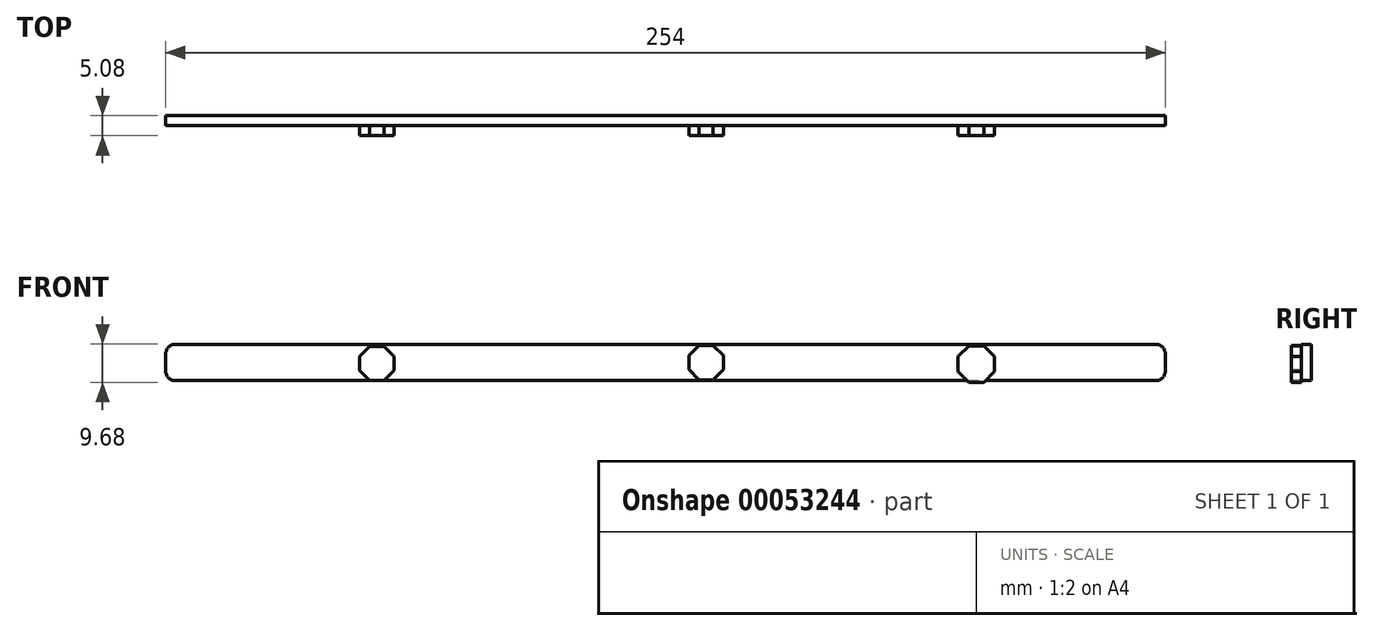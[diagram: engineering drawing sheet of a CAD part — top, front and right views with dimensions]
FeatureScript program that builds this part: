
annotation { "Feature Type Name" : "Feature", "Feature Type Description" : "" }
export const myFeature = defineFeature(function(context is Context, id is Id, definition is map)
    precondition{}
    {
        {
            var Q0;
            Q0=qCreatedBy(makeId("Front.planeOp"),FACE);
            var sketch = newSketch(context, id + "F0", { "sketchPlane" : qUnion([Q0])});
            skLineSegment(sketch, "E0.bottom", {"start": v(-129.82, 37.82) * mm, "end": v(124.18, 37.82) * mm});
            skLineSegment(sketch, "E0.top", {"start": v(-129.82, 28.55) * mm, "end": v(124.18, 28.55) * mm});
            skLineSegment(sketch, "E0.left", {"start": v(-129.82, 37.82) * mm, "end": v(-129.82, 28.55) * mm});
            skLineSegment(sketch, "E0.right", {"start": v(124.18, 37.82) * mm, "end": v(124.18, 28.55) * mm});
            skSolve(sketch);
        }
        {
            var Q0;
            Q0=makeQuery(id+"F0.imprint","IMPRINT",FACE,{"disambiguationData":[TD([[makeQuery(id+"F0.imprint","IMPRINT",EDGE,{"derivedFrom":sQuery(id+"F0.wireOp",EDGE,"E0.bottom")}),-1.0]])]});
            extrude(context, id + "F1", {"entities" : qUnion([Q0]), "depth" : 2.54 * mm});
        }
        {
            var Q0;
            Q0=makeQuery(id+"F1.opExtrude","SWEPT_EDGE",EDGE,{"disambiguationData":[OSD([sQuery(id+"F0.wireOp",EDGE,"E0.bottom"),sQuery(id+"F0.wireOp",EDGE,"E0.right")])]});
            var Q1;
            Q1=makeQuery(id+"F1.opExtrude","SWEPT_EDGE",EDGE,{"disambiguationData":[OSD([sQuery(id+"F0.wireOp",EDGE,"E0.top"),sQuery(id+"F0.wireOp",EDGE,"E0.right")])]});
            var Q2;
            Q2=makeQuery(id+"F1.opExtrude","SWEPT_EDGE",EDGE,{"disambiguationData":[OSD([sQuery(id+"F0.wireOp",EDGE,"E0.bottom"),sQuery(id+"F0.wireOp",EDGE,"E0.left")])]});
            var Q3;
            Q3=makeQuery(id+"F1.opExtrude","SWEPT_EDGE",EDGE,{"disambiguationData":[OSD([sQuery(id+"F0.wireOp",EDGE,"E0.top"),sQuery(id+"F0.wireOp",EDGE,"E0.left")])]});
            fillet(context, id + "F2", {"entities" : qUnion([Q0, Q1, Q2, Q3]), "radius" : 2.54 * mm, "tangentPropagation" : true, "allowEdgeOverflow" : false});
        }
        {
            var Q0;
            Q0=makeQuery(id+"F1.opExtrude","CAP_FACE",FACE,{"disambiguationData":[OSD([sQuery(id+"F0.wireOp",EDGE,"E0.bottom"),sQuery(id+"F0.wireOp",EDGE,"E0.top"),sQuery(id+"F0.wireOp",EDGE,"E0.left"),sQuery(id+"F0.wireOp",EDGE,"E0.right")])],"isStart":false});
            var sketch = newSketch(context, id + "F3", { "sketchPlane" : qUnion([Q0])});
            skCircle(sketch, "E1.cCircle", {"center": v(-76.18, 32.92) * mm, "radius": 4.37 * mm, "construction": true});
            skLineSegment(sketch, "E1.0", {"start": v(-74.37, 28.55) * mm, "end": v(-78, 28.55) * mm});
            skLineSegment(sketch, "E1.1", {"start": v(-78, 28.55) * mm, "end": v(-80.55, 31.1) * mm});
            skLineSegment(sketch, "E1.2", {"start": v(-80.55, 31.1) * mm, "end": v(-80.55, 34.73) * mm});
            skLineSegment(sketch, "E1.3", {"start": v(-80.55, 34.73) * mm, "end": v(-78, 37.3) * mm});
            skLineSegment(sketch, "E1.4", {"start": v(-78, 37.3) * mm, "end": v(-74.37, 37.3) * mm});
            skLineSegment(sketch, "E1.5", {"start": v(-74.37, 37.3) * mm, "end": v(-71.8, 34.73) * mm});
            skLineSegment(sketch, "E1.6", {"start": v(-71.8, 34.73) * mm, "end": v(-71.8, 31.1) * mm});
            skLineSegment(sketch, "E1.7", {"start": v(-71.8, 31.1) * mm, "end": v(-74.37, 28.55) * mm});
            skPoint(sketch, "E1.0.midPoint", {"position": v(-76.18, 28.55) * mm});
            skSolve(sketch);
        }
        {
            var Q0;
            {var subQ7=sQuery(id+"F3.wireOp",EDGE,"E1.1");Q0=makeQuery(id+"F3.imprint","IMPRINT",FACE,{"disambiguationData":[TD([[makeQuery(id+"F3.imprint","IMPRINT",EDGE,{"derivedFrom":subQ7}),1.0]])]});}
            var sketch = newSketch(context, id + "F4", { "sketchPlane" : qUnion([Q0])});
            skCircle(sketch, "E2.cCircle", {"center": v(7.47, 33.16) * mm, "radius": 4.38 * mm, "construction": true});
            skLineSegment(sketch, "E2.0", {"start": v(9.28, 28.78) * mm, "end": v(5.66, 28.78) * mm});
            skLineSegment(sketch, "E2.1", {"start": v(5.66, 28.78) * mm, "end": v(3.1, 31.35) * mm});
            skLineSegment(sketch, "E2.2", {"start": v(3.1, 31.35) * mm, "end": v(3.1, 34.97) * mm});
            skLineSegment(sketch, "E2.3", {"start": v(3.1, 34.97) * mm, "end": v(5.66, 37.54) * mm});
            skLineSegment(sketch, "E2.4", {"start": v(5.66, 37.54) * mm, "end": v(9.28, 37.54) * mm});
            skLineSegment(sketch, "E2.5", {"start": v(9.28, 37.54) * mm, "end": v(11.85, 34.97) * mm});
            skLineSegment(sketch, "E2.6", {"start": v(11.85, 34.97) * mm, "end": v(11.85, 31.35) * mm});
            skLineSegment(sketch, "E2.7", {"start": v(11.85, 31.35) * mm, "end": v(9.28, 28.78) * mm});
            skPoint(sketch, "E2.0.midPoint", {"position": v(7.47, 28.78) * mm});
            skSolve(sketch);
        }
        {
            var Q0;
            Q0=makeQuery(id+"F4.imprint","IMPRINT",FACE,{"disambiguationData":[TD([[makeQuery(id+"F4.imprint","IMPRINT",EDGE,{"derivedFrom":sQuery(id+"F4.wireOp",EDGE,"E2.0")}),1.0]])]});
            var sketch = newSketch(context, id + "F5", { "sketchPlane" : qUnion([Q0])});
            skCircle(sketch, "E3.cCircle", {"center": v(76.15, 32.78) * mm, "radius": 4.64 * mm, "construction": true});
            skLineSegment(sketch, "E3.0", {"start": v(78.07, 28.14) * mm, "end": v(74.22, 28.14) * mm});
            skLineSegment(sketch, "E3.1", {"start": v(74.22, 28.14) * mm, "end": v(71.5, 30.85) * mm});
            skLineSegment(sketch, "E3.2", {"start": v(71.5, 30.85) * mm, "end": v(71.5, 34.7) * mm});
            skLineSegment(sketch, "E3.3", {"start": v(71.5, 34.7) * mm, "end": v(74.22, 37.42) * mm});
            skLineSegment(sketch, "E3.4", {"start": v(74.22, 37.42) * mm, "end": v(78.07, 37.42) * mm});
            skLineSegment(sketch, "E3.5", {"start": v(78.07, 37.42) * mm, "end": v(80.79, 34.7) * mm});
            skLineSegment(sketch, "E3.6", {"start": v(80.79, 34.7) * mm, "end": v(80.79, 30.85) * mm});
            skLineSegment(sketch, "E3.7", {"start": v(80.79, 30.85) * mm, "end": v(78.07, 28.14) * mm});
            skPoint(sketch, "E3.0.midPoint", {"position": v(76.15, 28.14) * mm});
            skSolve(sketch);
        }
        {
            var Q0;
            Q0=makeQuery(id+"F3.imprint","IMPRINT",FACE,{"disambiguationData":[TD([[makeQuery(id+"F3.imprint","IMPRINT",EDGE,{"derivedFrom":sQuery(id+"F3.wireOp",EDGE,"E1.0")}),1.0]])]});
            var Q1;
            Q1=makeQuery(id+"F4.imprint","IMPRINT",FACE,{"disambiguationData":[TD([[makeQuery(id+"F4.imprint","IMPRINT",EDGE,{"derivedFrom":sQuery(id+"F4.wireOp",EDGE,"E2.0")}),-1.0]])]});
            var Q2;
            {var subQ0=sQuery(id+"F5.wireOp",EDGE,"E3.0");Q2=makeQuery(id+"F5.imprint","IMPRINT",FACE,{"disambiguationData":[TD([[makeQuery(id+"F5.imprint","IMPRINT",EDGE,{"derivedFrom":subQ0}),-1.0]])]});}
            var Q3;
            {var subQ7=sQuery(id+"F5.wireOp",EDGE,"E3.2");Q3=makeQuery(id+"F5.imprint","IMPRINT",FACE,{"disambiguationData":[TD([[makeQuery(id+"F5.imprint","IMPRINT",EDGE,{"derivedFrom":subQ7}),-1.0]])]});}
            extrude(context, id + "F6", {"entities" : qUnion([Q0, Q1, Q2, Q3]), "operationType" : NewBodyOperationType.ADD, "depth" : 2.54 * mm});
        }
    });
